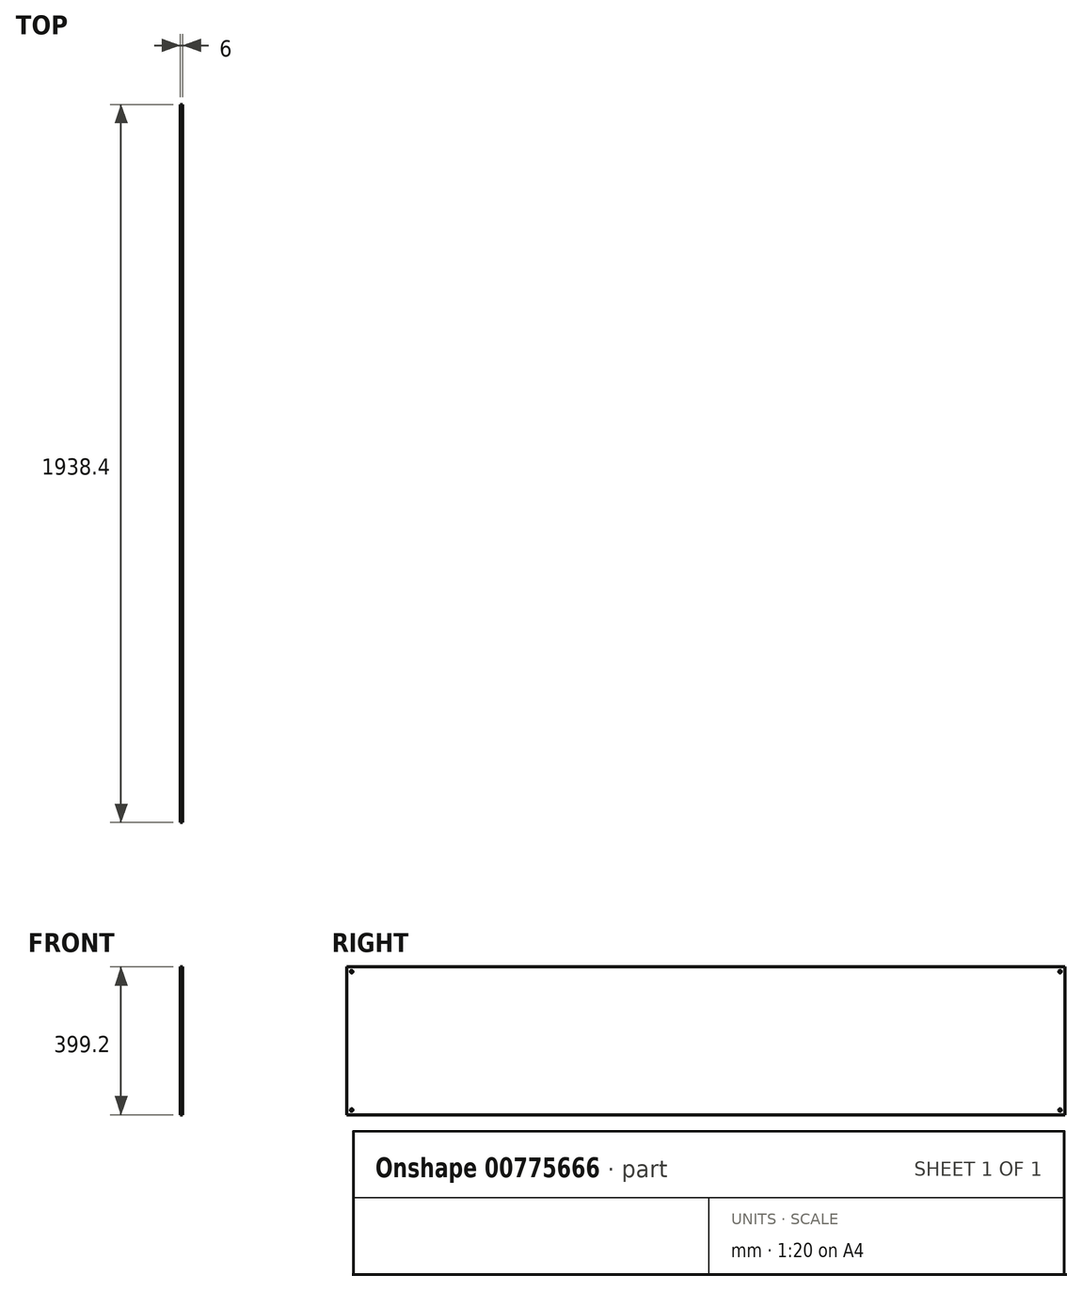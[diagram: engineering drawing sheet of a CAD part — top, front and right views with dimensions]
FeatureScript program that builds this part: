
annotation { "Feature Type Name" : "Feature", "Feature Type Description" : "" }
export const myFeature = defineFeature(function(context is Context, id is Id, definition is map)
    precondition{}
    {
        {
            var Q0;
            Q0=qCreatedBy(makeId("Right.planeOp"),FACE);
            var sketch = newSketch(context, id + "F0", { "sketchPlane" : qUnion([Q0])});
            skLineSegment(sketch, "E0.bottom", {"start": v(969.2, 199.6) * mm, "end": v(-969.2, 199.6) * mm});
            skLineSegment(sketch, "E0.top", {"start": v(969.2, -199.6) * mm, "end": v(-969.2, -199.6) * mm});
            skLineSegment(sketch, "E0.left", {"start": v(969.2, 199.6) * mm, "end": v(969.2, -199.6) * mm});
            skLineSegment(sketch, "E0.right", {"start": v(-969.2, 199.6) * mm, "end": v(-969.2, -199.6) * mm});
            skPoint(sketch, "E0.middle", {"position": v(0, 0) * mm});
            skSolve(sketch);
        }
        {
            var Q0;
            Q0=makeQuery(id+"F0.imprint","IMPRINT",FACE,{"disambiguationData":[TD([[makeQuery(id+"F0.imprint","IMPRINT",EDGE,{"derivedFrom":sQuery(id+"F0.wireOp",EDGE,"E0.bottom")}),1.0]])]});
            extrude(context, id + "F1", {"entities" : qUnion([Q0]), "depth" : 6 * mm, "offsetDistance" : 25 * mm});
        }
        {
            var Q0;
            Q0=makeQuery(id+"F1.opExtrude","CAP_FACE",FACE,{"disambiguationData":[OSD([sQuery(id+"F0.wireOp",EDGE,"E0.bottom"),sQuery(id+"F0.wireOp",EDGE,"E0.top"),sQuery(id+"F0.wireOp",EDGE,"E0.left"),sQuery(id+"F0.wireOp",EDGE,"E0.right")])],"isStart":false});
            var sketch = newSketch(context, id + "F2", { "sketchPlane" : qUnion([Q0])});
            skPoint(sketch, "E1", {"position": v(-956.5, 186.9) * mm});
            skPoint(sketch, "E2", {"position": v(-956.5, -186.9) * mm});
            skPoint(sketch, "E3", {"position": v(956.5, -186.9) * mm});
            skPoint(sketch, "E4", {"position": v(956.5, 186.9) * mm});
            skSolve(sketch);
        }
        {
            var Q0;
            Q0=sQuery(id+"F2.wireOp",VERTEX,"E1");
            var Q1;
            Q1=sQuery(id+"F2.wireOp",VERTEX,"E2");
            var Q2;
            Q2=sQuery(id+"F2.wireOp",VERTEX,"E4");
            var Q3;
            Q3=sQuery(id+"F2.wireOp",VERTEX,"E3");
            var Q4;
            Q4=makeQuery(id+"F1.opExtrude","SWEPT_BODY",BODY,{"disambiguationData":[OSD([sQuery(id+"F0.wireOp",EDGE,"E0.bottom"),sQuery(id+"F0.wireOp",EDGE,"E0.top"),sQuery(id+"F0.wireOp",EDGE,"E0.left"),sQuery(id+"F0.wireOp",EDGE,"E0.right")])]});
            hole(context, id + "F3", {"style" : HoleStyle.SIMPLE, "endStyle" : HoleEndStyle.BLIND, "holeDiameter" : 7 * mm, "majorDiameter" : 5 * mm, "holeDepth" : 100 * mm, "isTappedThrough" : true, "tappedDepth" : 12 * mm, "tapClearance" : 3, "locations" : qUnion([Q0, Q1, Q2, Q3]), "scope" : qUnion([Q4])});
        }
    });
